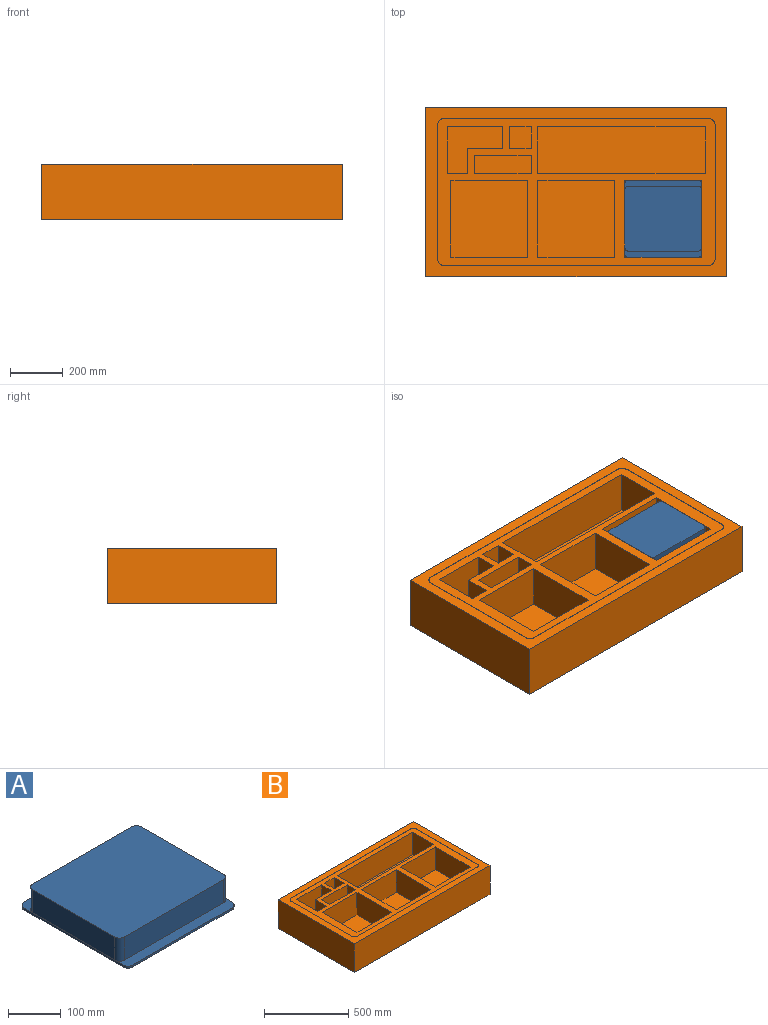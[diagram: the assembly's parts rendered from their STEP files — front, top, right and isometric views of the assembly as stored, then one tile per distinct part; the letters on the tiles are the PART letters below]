
ASSEMBLY  parts=2 mates=1
PART A: 29 faces, bbox 292.1x292.1x96.6 mm
  f0: plane 266.7x4.83mm, normal (1,0,0), area 1287.1mm2, adj f1,f7,f8,f9
  f1: cylinder r=12.7mm len=12.7mm, axis (0,0,-1), area 96.3mm2, adj f0,f2,f8,f9
  f2: plane 266.7x4.83mm, normal (0,1,0), area 1287.1mm2, adj f1,f3,f8,f9
  f3: cylinder r=12.7mm len=12.7mm, axis (0,0,-1), area 96.3mm2, adj f2,f4,f8,f9
  f4: plane 266.7x4.83mm, normal (-1,0,0), area 1287.1mm2, adj f3,f5,f8,f9
  f5: cylinder r=12.7mm len=12.7mm, axis (0,0,-1), area 96.3mm2, adj f4,f6,f8,f9
  f6: plane 266.7x4.83mm, normal (0,-1,0), area 1287.1mm2, adj f5,f7,f8,f9
  f7: cylinder r=12.7mm len=12.7mm, axis (0,0,-1), area 96.3mm2, adj f0,f6,f8,f9
  f8: plane 292.1x292.1mm, normal (0,0,1), area 13627.3mm2, adj f0,f1,f2,f3,f4,f5,f6,f7
  f9: plane 292.1x292.1mm, normal (0,0,-1), area 84677.2mm2, adj f0,f1,f2,f3,f4,f5,f6,f7
  f10: cylinder r=6.35mm len=19.05mm, axis (0,0,1), area 760.1mm2, adj f9,f14
  f11: cylinder r=6.35mm len=19.05mm, axis (0,0,1), area 760.1mm2, adj f9,f14
  f12: cylinder r=6.35mm len=19.05mm, axis (0,0,1), area 760.1mm2, adj f9,f14
  f13: cylinder r=6.35mm len=19.05mm, axis (0,0,1), area 760.1mm2, adj f9,f14
  f14: plane 85.09x50.8mm, normal (0,0,1), area 3815.9mm2, adj f10,f11,f12,f13,f15,f16,f17,f18
  f15: plane 85.09x19.05mm, normal (-1,0,0), area 1621mm2, adj f14,f16,f18,f19
  f16: plane 50.8x19.05mm, normal (0,-1,0), area 967.7mm2, adj f14,f15,f17,f19
  f17: plane 85.09x19.05mm, normal (1,0,0), area 1621mm2, adj f14,f16,f18,f19
  f18: plane 50.8x19.05mm, normal (0,1,0), area 967.7mm2, adj f14,f15,f17,f19
  f19: plane 85.09x50.8mm, normal (0,0,-1), area 4322.6mm2, adj f15,f16,f17,f18
  f20: plane 220.3x53.7mm, normal (1,0,0), area 11830.2mm2, adj f8,f21,f27,f28
  f21: cylinder r=12.7mm len=53.7mm, axis (0,0,-1), area 1071.3mm2, adj f8,f20,f22,f28
  f22: plane 266.4x53.7mm, normal (0,1,0), area 14305.9mm2, adj f8,f21,f23,f28
  f23: cylinder r=12.7mm len=53.7mm, axis (0,0,-1), area 1071.3mm2, adj f8,f22,f24,f28
  f24: plane 220.3x53.7mm, normal (-1,0,0), area 11830.2mm2, adj f8,f23,f25,f28
  f25: cylinder r=12.7mm len=53.7mm, axis (0,0,-1), area 1071.3mm2, adj f8,f24,f26,f28
  f26: plane 266.4x53.7mm, normal (0,-1,0), area 14305.9mm2, adj f8,f25,f27,f28
  f27: cylinder r=12.7mm len=53.7mm, axis (0,0,-1), area 1071.3mm2, adj f8,f20,f26,f28
  f28: plane 291.8x245.7mm, normal (0,0,1), area 71556.7mm2, adj f20,f21,f22,f23,f24,f25,f26,f27
PART B: 52 faces, bbox 1140.5x643.1x209.6 mm
  f0: plane 292.1x165.1mm, normal (0,1,0), area 48225.7mm2, adj f9,f27,f42,f44
  f1: plane 292.1x165.1mm, normal (0,1,0), area 48225.7mm2, adj f8,f27,f45,f47
  f2: plane 292.1x165.1mm, normal (0,1,0), area 48225.7mm2, adj f7,f27,f32,f48
  f3: plane 177.8x165.1mm, normal (1,0,0), area 29354.8mm2, adj f26,f27,f28,f41
  f4: plane 635x165.1mm, normal (0,-1,0), area 104838.5mm2, adj f6,f11,f27,f34
  f5: plane 165.1x82.55mm, normal (0,-1,0), area 13629mm2, adj f10,f27,f35,f37
  f6: plane 177.8x165.1mm, normal (-1,0,0), area 29354.8mm2, adj f4,f11,f27,f33
  f7: plane 292.1x292.1mm, normal (0,0,1), area 85322.4mm2, adj f2,f32,f48,f49
  f8: plane 292.1x292.1mm, normal (0,0,1), area 85322.4mm2, adj f1,f45,f46,f47
  f9: plane 292.1x292.1mm, normal (0,0,1), area 85322.4mm2, adj f0,f42,f43,f44
  f10: plane 82.55x82.55mm, normal (0,0,1), area 6814.5mm2, adj f5,f35,f36,f37
  f11: plane 635x177.8mm, normal (0,0,1), area 112903mm2, adj f4,f6,f33,f34
  f12: plane 508x1.27mm, normal (-1,0,0), area 645.2mm2, adj f16,f19,f24,f27
  f13: plane 1003.3x1.27mm, normal (0,-1,0), area 1274.2mm2, adj f16,f17,f24,f27
  f14: plane 508x1.27mm, normal (1,0,0), area 645.2mm2, adj f17,f18,f24,f27
  f15: plane 1003.3x1.27mm, normal (0,1,0), area 1274.2mm2, adj f18,f19,f24,f27
  f16: cylinder r=25.4mm len=25.4mm, axis (0,0,1), area 50.7mm2, adj f12,f13,f24,f27
  f17: cylinder r=25.4mm len=25.4mm, axis (0,0,1), area 50.7mm2, adj f13,f14,f24,f27
  f18: cylinder r=25.4mm len=25.4mm, axis (0,0,1), area 50.7mm2, adj f14,f15,f24,f27
  f19: cylinder r=25.4mm len=25.4mm, axis (0,0,1), area 50.7mm2, adj f12,f15,f24,f27
  f20: plane 643.13x209.55mm, normal (-1,0,0), area 134767.5mm2, adj f21,f23,f24,f25
  f21: plane 1140.46x209.55mm, normal (0,-1,0), area 238983.4mm2, adj f20,f22,f24,f25
  f22: plane 643.13x209.55mm, normal (1,0,0), area 134767.5mm2, adj f21,f23,f24,f25
  f23: plane 1140.46x209.55mm, normal (0,1,0), area 238983.4mm2, adj f20,f22,f24,f25
  f24: plane 1140.46x643.13mm, normal (0,0,1), area 144984.5mm2, adj f12,f13,f14,f15,f16,f17,f18,f19
  f25: plane 1140.46x643.13mm, normal (0,0,-1), area 733461.8mm2, adj f20,f21,f22,f23
  f26: plane 209.55x165.1mm, normal (0,-1,0), area 34596.7mm2, adj f3,f27,f28,f38
  f27: plane 1054.1x558.8mm, normal (0,0,1), area 173155.5mm2, adj f0,f1,f2,f3,f4,f5,f6,f12
  f28: plane 209.55x177.8mm, normal (0,0,1), area 24556.4mm2, adj f3,f26,f38,f39,f40,f41
  f29: plane 215.9x165.1mm, normal (0,-1,0), area 35645.1mm2, adj f27,f30,f50,f51
  f30: plane 165.1x69.85mm, normal (-1,0,0), area 11532.2mm2, adj f27,f29,f31,f51
  f31: plane 215.9x165.1mm, normal (0,1,0), area 35645.1mm2, adj f27,f30,f50,f51
  f32: plane 292.1x165.1mm, normal (-1,0,0), area 48225.7mm2, adj f2,f7,f27,f49
  f33: plane 635x165.1mm, normal (0,1,0), area 104838.5mm2, adj f6,f11,f27,f34
  f34: plane 177.8x165.1mm, normal (1,0,0), area 29354.8mm2, adj f4,f11,f27,f33
  f35: plane 165.1x82.55mm, normal (-1,0,0), area 13629mm2, adj f5,f10,f27,f36
  f36: plane 165.1x82.55mm, normal (0,1,0), area 13629mm2, adj f10,f27,f35,f37
  f37: plane 165.1x82.55mm, normal (1,0,0), area 13629mm2, adj f5,f10,f27,f36
  f38: plane 165.1x82.55mm, normal (-1,0,0), area 13629mm2, adj f26,f27,f28,f39
  f39: plane 165.1x133.35mm, normal (0,1,0), area 22016.1mm2, adj f27,f28,f38,f40
  f40: plane 165.1x95.25mm, normal (-1,0,0), area 15725.8mm2, adj f27,f28,f39,f41
  f41: plane 165.1x76.2mm, normal (0,1,0), area 12580.6mm2, adj f3,f27,f28,f40
  f42: plane 292.1x165.1mm, normal (1,0,0), area 48225.7mm2, adj f0,f9,f27,f43
  f43: plane 292.1x165.1mm, normal (0,-1,0), area 48225.7mm2, adj f9,f27,f42,f44
  f44: plane 292.1x165.1mm, normal (-1,0,0), area 48225.7mm2, adj f0,f9,f27,f43
  f45: plane 292.1x165.1mm, normal (1,0,0), area 48225.7mm2, adj f1,f8,f27,f46
  f46: plane 292.1x165.1mm, normal (0,-1,0), area 48225.7mm2, adj f8,f27,f45,f47
  f47: plane 292.1x165.1mm, normal (-1,0,0), area 48225.7mm2, adj f1,f8,f27,f46
  f48: plane 292.1x165.1mm, normal (1,0,0), area 48225.7mm2, adj f2,f7,f27,f49
  f49: plane 292.1x165.1mm, normal (0,-1,0), area 48225.7mm2, adj f7,f27,f32,f48
  f50: plane 165.1x69.85mm, normal (1,0,0), area 11532.2mm2, adj f27,f29,f31,f51
  f51: plane 215.9x69.85mm, normal (0,0,1), area 15080.6mm2, adj f29,f30,f31,f50
PLACE A t=(589.11,865.94,778.25)mm
PLACE B t=(-268.14,688.14,630.93)mm
MATE slider B.f7 <-> A.f19  axis (0,0,1) through (589.11,865.94,674.11)mm
